# Revit family: IS_Multisuite_T6820_BIM_ES
name_source: partatom
category: Plumbing Fixtures
revit_build: Autodesk Revit MEP 2014 (Build: 20130308_1515(x64)
units: mm (PartAtom-declared; Revit-internal decimal feet)

## types (1)
- T682067 - PLASTIC ELBOW HO/VO 90MM DIAM+FIXATIONS
    Acabado = Blanco
    Accesorios = www.idealstandard.es
    Altura = 303 mm
    Anchura = 137 mm
    Autor = Ideal Standard s.l.u. (ESP)
    Color = 0
    CódigoDeBarras = 8014140406877
    Default Elevation = 0 mm  [stored 0 ft]
    Description = 0
    Destacado = 0
    Dimensiones = 194 x 137 x 303 mm
    Espacio = Interno
    FechaDeCreación = 2017-01-28
    Forma = Escultural
    GarantíaDeLasPiezas = www.idealstandard.es
    GarantíaPiezas = 2
    GuíaDeInstallación = www.idealstandard.es
    InformaciónDeProducto = www.idealstandard.es
    Longitud = 194 mm
    Manufacturer = www.idealstandard.es
    Marca = Ideal Standard
    Material = 0
    Model = T682067
    Nombre = Ancillaries_Ancillary_T682067_IdealStandard
    NombreDeObjetoBim = IdealStandard_Ancillaries_Ancillary_T682067
    NúmeroDeModelo = T682067
    PesoBruto = 0
    PesoNeto = 0.50 Kg
    Profundidad = 0 mm  [stored 0 ft]
    Repuestos = www.idealstandard.es
    Teléfono = 935 618 000
    TipoDeConexión = Instalación
    TipoDeGarantía = Garantía del Fabricante
    URL = www.idealstandard.es
    UnidadDeVolúmen = Litros
    UnidadDeÁrea = milímetros
    UnidadGarantía = año
    UnidadLineal = milímetros
    Versión = 1

note: [stored X ft] marks values corroborated as IEEE doubles in the binary element streams (Revit-internal decimal feet)

## geometry (parser evidence)
native form markers: Sweep x2
no freeform markers — native parametric forms only
